# Revit family: 7cc5859f-332f-4849-8e5e-45946143b131
name_source: partatom
category: Plumbing Fixtures
revit_build: Autodesk Revit 2016 (Build: 20161004_0715(x64)
units: mm (PartAtom-declared; Revit-internal decimal feet)

## family parameters
Cut with Voids When Loaded = No
Host = Face
OmniClass Number = 23.45.05.21.11.11
OmniClass Title = Water Operated Water Closets
Part Type = Normal
Room Calculation Point = No
Round Connector Dimension = Use Radius
Shared = No

## types (7) — shared parameters
Assembly Code = D2010110
CW Connection = Yes
Cold Water Connection = Cold Water Connector
Cold Water Diameter = 0"
Cold Water Radius = 0"
Default Elevation = 0' - 0"
Description = Memoirs® Comfort Height® two piece elongated 1.6 gpf toilet with Classic design
Flush Rate = 1.6 GPM
HW Connection = No
Manufacturer = Kohler
Model = K-3818
Product Documentation Link = http://www.us.kohler.com
Product Page URL = http://www.us.kohler.com
Rough In = 1' - 0"
Sanitary Connection = Sanitary Connector
Sanitary Diameter = 3"
Sanitary Radius = 2"
Type Image = <None>
URL = http://www.us.kohler.com
Vent Connection = No
Wall Offset = 0' - 0 1/2"
Waste Connection = Yes
zero-valued in all types: CWFU, WFU

## per-type parameters (varying)
| type | Finish |
| Vitreous_China-0-White | Vitreous China-Kohler-0-White |
| Vitreous_China-7-Black_Black | Vitreous China-Kohler-7-Black Black |
| Vitreous_China-47-Almond | Vitreous China-Kohler-47-Almond |
| Vitreous_China-95-Ice_Grey | Vitreous China-Kohler-95-Ice Grey |
| Vitreous_China-96-Biscuit | Vitreous China-Kohler-96-Biscuit |
| Vitreous_China-G9-Sandbar | Vitreous China-Kohler-G9-Sandbar |
| Vitreous_China-NY-Dune | Vitreous China-Kohler-NY-Dune |

## geometry (parser evidence)
native form markers: Blend x30, Sweep x5
no freeform markers — native parametric forms only
